# Revit family: Ribbstol Large sammansatt
name_source: partatom
category: Generic Models
revit_build: Autodesk Revit 2017 (Build: 20160225_1515(x64)
units: mm (PartAtom-declared; Revit-internal decimal feet)

## family parameters
Always vertical = Yes
Can host rebar = No
Cut with Voids When Loaded = No
Part Type = Normal
Room Calculation Point = No
Round Connector Dimension = Use Diameter
Shared = No
Work Plane-Based = No

## types (10) — shared parameters
Manufacturer = Saxi Vägg AB
Model = Ribbstol Large
URL = www.saxi.se

## per-type parameters (varying)
| type | 1facksynlung | ANTAL_FACK | SYNLIG | langd_barande | langd_list |
| Saxi Ribbstol Large 1-fack | Yes | 2 | No | 1857 mm | 1657 mm |
| Saxi Ribbstol Large 2-fack | No | 2 | Yes | 1857 mm | 1657 mm |
| Saxi Ribbstol Large 3-fack | No | 3 | Yes | 2639 mm | 2439 mm |
| Saxi Ribbstol Large 4-fack | No | 4 | Yes | 3421 mm | 3221 mm |
| Saxi Ribbstol Large 5-fack | No | 5 | Yes | 4203 mm  [stored 13.7894 ft] | 4003 mm  [stored 13.1332 ft] |
| Saxi Ribbstol Large 6-fack | No | 6 | Yes | 4985 mm  [stored 16.355 ft] | 4785 mm |
| Saxi Ribbstol Large 7-fack | No | 7 | Yes | 5767 mm | 5567 mm |
| Saxi Ribbstol Large 8-fack | No | 8 | Yes | 6549 mm | 6349 mm |
| Saxi Ribbstol Large 9-fack | No | 9 | Yes | 7331 mm | 7131 mm |
| Saxi Ribbstol Large 10-fack | No | 10 | Yes | 8113 mm | 7913 mm |

note: [stored X ft] marks values corroborated as IEEE doubles in the binary element streams (Revit-internal decimal feet)

## geometry (parser evidence)
native form markers: Sweep x17
no freeform markers — native parametric forms only
